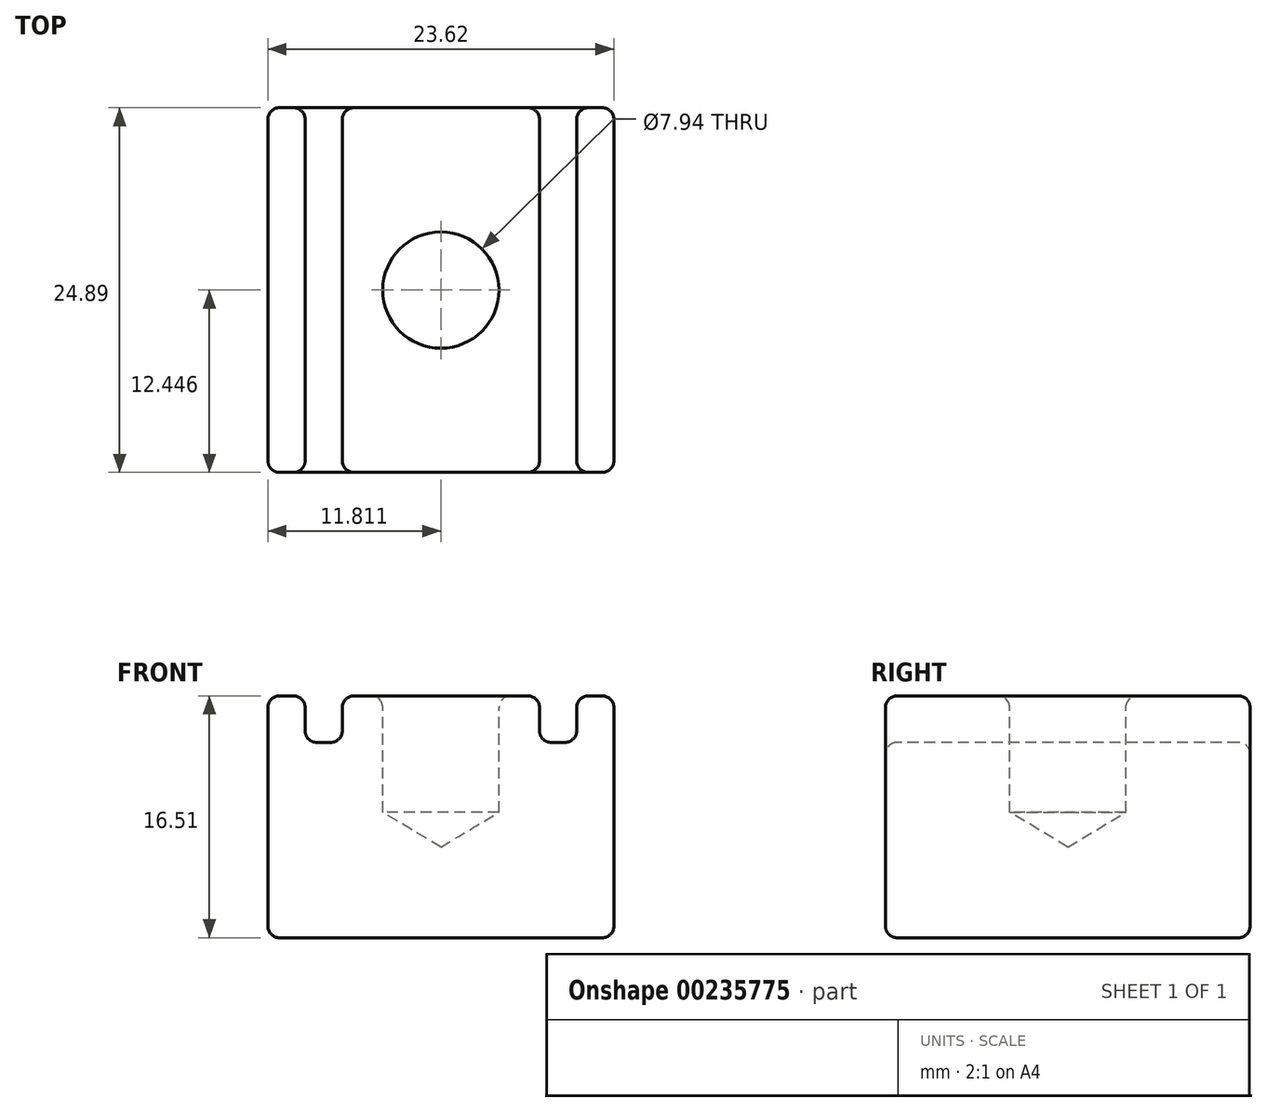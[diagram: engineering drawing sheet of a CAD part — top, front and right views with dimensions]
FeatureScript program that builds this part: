
annotation { "Feature Type Name" : "Feature", "Feature Type Description" : "" }
export const myFeature = defineFeature(function(context is Context, id is Id, definition is map)
    precondition{}
    {
        {
            var Q0;
            Q0=qCreatedBy(makeId("Top.planeOp"),FACE);
            var sketch = newSketch(context, id + "F0", { "sketchPlane" : qUnion([Q0])});
            skLineSegment(sketch, "E0.bottom", {"start": v(0.8, 0) * mm, "end": v(1.75, 0) * mm});
            skLineSegment(sketch, "E0.top", {"start": v(0.8, 24.9) * mm, "end": v(1.75, 24.9) * mm});
            skLineSegment(sketch, "E0.left", {"start": v(0, 0.8) * mm, "end": v(0, 24.1) * mm});
            skLineSegment(sketch, "E0.right", {"start": v(2.54, 0.8) * mm, "end": v(2.54, 24.1) * mm});
            skPoint(sketch, "E1.visualSharp", {"position": v(0, 24.9) * mm});
            skArc(sketch, "E1.filletArc", {"start": v(0.8, 24.9) * mm, "mid": v(0.23, 24.66) * mm, "end": v(0, 24.1) * mm});
            skPoint(sketch, "E2.visualSharp", {"position": v(0, 0) * mm});
            skArc(sketch, "E2.filletArc", {"start": v(0, 0.8) * mm, "mid": v(0.23, 0.23) * mm, "end": v(0.8, 0) * mm});
            skPoint(sketch, "E3.visualSharp", {"position": v(2.54, 24.9) * mm});
            skArc(sketch, "E3.filletArc", {"start": v(2.54, 24.1) * mm, "mid": v(2.3, 24.66) * mm, "end": v(1.75, 24.9) * mm});
            skPoint(sketch, "E4.visualSharp", {"position": v(2.54, 0) * mm});
            skArc(sketch, "E4.filletArc", {"start": v(1.75, 0) * mm, "mid": v(2.3, 0.23) * mm, "end": v(2.54, 0.8) * mm});
            skLineSegment(sketch, "E5.bottom", {"start": v(21.88, 0) * mm, "end": v(22.83, 0) * mm});
            skLineSegment(sketch, "E5.top", {"start": v(21.88, 24.9) * mm, "end": v(22.83, 24.9) * mm});
            skLineSegment(sketch, "E5.left", {"start": v(21.08, 0.8) * mm, "end": v(21.08, 24.1) * mm});
            skLineSegment(sketch, "E5.right", {"start": v(23.62, 0.8) * mm, "end": v(23.62, 24.1) * mm});
            skPoint(sketch, "E6.visualSharp", {"position": v(21.08, 24.9) * mm});
            skArc(sketch, "E6.filletArc", {"start": v(21.88, 24.9) * mm, "mid": v(21.31, 24.66) * mm, "end": v(21.08, 24.1) * mm});
            skPoint(sketch, "E7.visualSharp", {"position": v(21.08, 0) * mm});
            skArc(sketch, "E7.filletArc", {"start": v(21.08, 0.8) * mm, "mid": v(21.31, 0.23) * mm, "end": v(21.88, 0) * mm});
            skPoint(sketch, "E8.visualSharp", {"position": v(23.62, 24.9) * mm});
            skArc(sketch, "E8.filletArc", {"start": v(23.62, 24.1) * mm, "mid": v(23.39, 24.66) * mm, "end": v(22.83, 24.9) * mm});
            skPoint(sketch, "E9.visualSharp", {"position": v(23.62, 0) * mm});
            skArc(sketch, "E9.filletArc", {"start": v(22.83, 0) * mm, "mid": v(23.39, 0.23) * mm, "end": v(23.62, 0.8) * mm});
            skLineSegment(sketch, "E10.bottom", {"start": v(5.87, 24.9) * mm, "end": v(17.75, 24.9) * mm});
            skLineSegment(sketch, "E10.top", {"start": v(5.87, 0) * mm, "end": v(17.75, 0) * mm});
            skLineSegment(sketch, "E10.left", {"start": v(5.08, 24.1) * mm, "end": v(5.08, 0.8) * mm});
            skLineSegment(sketch, "E10.right", {"start": v(18.54, 24.1) * mm, "end": v(18.54, 0.8) * mm});
            skPoint(sketch, "E11.visualSharp", {"position": v(5.08, 24.9) * mm});
            skArc(sketch, "E11.filletArc", {"start": v(5.87, 24.9) * mm, "mid": v(5.31, 24.66) * mm, "end": v(5.08, 24.1) * mm});
            skPoint(sketch, "E12.visualSharp", {"position": v(18.54, 24.9) * mm});
            skArc(sketch, "E12.filletArc", {"start": v(18.54, 24.1) * mm, "mid": v(18.3, 24.66) * mm, "end": v(17.75, 24.9) * mm});
            skPoint(sketch, "E13.visualSharp", {"position": v(18.54, 0) * mm});
            skArc(sketch, "E13.filletArc", {"start": v(17.75, 0) * mm, "mid": v(18.3, 0.23) * mm, "end": v(18.54, 0.8) * mm});
            skPoint(sketch, "E14.visualSharp", {"position": v(5.08, 0) * mm});
            skArc(sketch, "E14.filletArc", {"start": v(5.08, 0.8) * mm, "mid": v(5.31, 0.23) * mm, "end": v(5.87, 0) * mm});
            skSolve(sketch);
        }
        {
            var Q0;
            Q0=qCreatedBy(makeId("Top.planeOp"),FACE);
            var sketch = newSketch(context, id + "F1", { "sketchPlane" : qUnion([Q0])});
            skLineSegment(sketch, "E15.bottom", {"start": v(0.8, 0) * mm, "end": v(22.83, 0) * mm});
            skLineSegment(sketch, "E15.top", {"start": v(0.8, 24.9) * mm, "end": v(22.83, 24.9) * mm});
            skLineSegment(sketch, "E15.left", {"start": v(0, 0.8) * mm, "end": v(0, 24.1) * mm});
            skLineSegment(sketch, "E15.right", {"start": v(23.62, 0.8) * mm, "end": v(23.62, 24.1) * mm});
            skPoint(sketch, "E16.visualSharp", {"position": v(0, 24.9) * mm});
            skArc(sketch, "E16.filletArc", {"start": v(0.8, 24.9) * mm, "mid": v(0.23, 24.66) * mm, "end": v(0, 24.1) * mm});
            skPoint(sketch, "E17.visualSharp", {"position": v(23.62, 24.9) * mm});
            skArc(sketch, "E17.filletArc", {"start": v(23.62, 24.1) * mm, "mid": v(23.39, 24.66) * mm, "end": v(22.83, 24.9) * mm});
            skPoint(sketch, "E18.visualSharp", {"position": v(23.62, 0) * mm});
            skArc(sketch, "E18.filletArc", {"start": v(22.83, 0) * mm, "mid": v(23.39, 0.23) * mm, "end": v(23.62, 0.8) * mm});
            skPoint(sketch, "E19.visualSharp", {"position": v(0, 0) * mm});
            skArc(sketch, "E19.filletArc", {"start": v(0, 0.8) * mm, "mid": v(0.23, 0.23) * mm, "end": v(0.8, 0) * mm});
            skSolve(sketch);
        }
        {
            var Q0;
            Q0 = qSketchRegion(id + "F1", true);
            extrude(context, id + "F2", {"entities" : qUnion([Q0]), "oppositeDirection" : true, "depth" : 13.33 * mm});
        }
        {
            var Q0;
            Q0 = qSketchRegion(id + "F0", true);
            extrude(context, id + "F3", {"entities" : qUnion([Q0]), "operationType" : NewBodyOperationType.ADD, "depth" : 3.17 * mm});
        }
        {
            var Q0;
            Q0=makeQuery(id+"F3.opExtrude","CAP_FACE",FACE,{"disambiguationData":[OSD([sQuery(id+"F0.wireOp",EDGE,"E10.bottom"),sQuery(id+"F0.wireOp",EDGE,"E10.top"),sQuery(id+"F0.wireOp",EDGE,"E10.left"),sQuery(id+"F0.wireOp",EDGE,"E10.right"),sQuery(id+"F0.wireOp",EDGE,"E11.filletArc"),sQuery(id+"F0.wireOp",EDGE,"E12.filletArc"),sQuery(id+"F0.wireOp",EDGE,"E13.filletArc"),sQuery(id+"F0.wireOp",EDGE,"E14.filletArc")])],"isStart":false});
            var sketch = newSketch(context, id + "F4", { "sketchPlane" : qUnion([Q0])});
            skCircle(sketch, "E20", {"center": v(11.81, 12.45) * mm, "radius": 3.97 * mm});
            skSolve(sketch);
        }
        {
            var Q0;
            Q0=sQuery(id+"F4.wireOp",VERTEX,"E20.center");
            var Q1;
            Q1=makeQuery(id+"F2.opExtrude","SWEPT_BODY",BODY,{"disambiguationData":[OSD([sQuery(id+"F1.wireOp",EDGE,"E15.bottom"),sQuery(id+"F1.wireOp",EDGE,"E15.top"),sQuery(id+"F1.wireOp",EDGE,"E15.left"),sQuery(id+"F1.wireOp",EDGE,"E15.right"),sQuery(id+"F1.wireOp",EDGE,"E16.filletArc"),sQuery(id+"F1.wireOp",EDGE,"E17.filletArc"),sQuery(id+"F1.wireOp",EDGE,"E18.filletArc"),sQuery(id+"F1.wireOp",EDGE,"E19.filletArc")])]});
            hole(context, id + "F5", {"style" : HoleStyle.SIMPLE, "endStyle" : HoleEndStyle.BLIND, "holeDiameter" : 7.94 * mm, "holeDepth" : 7.94 * mm, "locations" : qUnion([Q0]), "scope" : qUnion([Q1])});
        }
        {
            var Q0;
            Q0=makeQuery(id+"F3.opExtrude","CAP_FACE",FACE,{"disambiguationData":[OSD([sQuery(id+"F0.wireOp",EDGE,"E10.bottom"),sQuery(id+"F0.wireOp",EDGE,"E10.top"),sQuery(id+"F0.wireOp",EDGE,"E10.left"),sQuery(id+"F0.wireOp",EDGE,"E10.right"),sQuery(id+"F0.wireOp",EDGE,"E11.filletArc"),sQuery(id+"F0.wireOp",EDGE,"E12.filletArc"),sQuery(id+"F0.wireOp",EDGE,"E13.filletArc"),sQuery(id+"F0.wireOp",EDGE,"E14.filletArc")])],"isStart":false});
            var Q1;
            Q1=makeQuery(id+"F3.opExtrude","CAP_FACE",FACE,{"disambiguationData":[OSD([sQuery(id+"F0.wireOp",EDGE,"E5.bottom"),sQuery(id+"F0.wireOp",EDGE,"E5.top"),sQuery(id+"F0.wireOp",EDGE,"E5.left"),sQuery(id+"F0.wireOp",EDGE,"E5.right"),sQuery(id+"F0.wireOp",EDGE,"E6.filletArc"),sQuery(id+"F0.wireOp",EDGE,"E7.filletArc"),sQuery(id+"F0.wireOp",EDGE,"E8.filletArc"),sQuery(id+"F0.wireOp",EDGE,"E9.filletArc")])],"isStart":false});
            var Q2;
            Q2=makeQuery(id+"F3.opExtrude","CAP_FACE",FACE,{"disambiguationData":[OSD([sQuery(id+"F0.wireOp",EDGE,"E0.bottom"),sQuery(id+"F0.wireOp",EDGE,"E0.top"),sQuery(id+"F0.wireOp",EDGE,"E0.left"),sQuery(id+"F0.wireOp",EDGE,"E0.right"),sQuery(id+"F0.wireOp",EDGE,"E1.filletArc"),sQuery(id+"F0.wireOp",EDGE,"E2.filletArc"),sQuery(id+"F0.wireOp",EDGE,"E3.filletArc"),sQuery(id+"F0.wireOp",EDGE,"E4.filletArc")])],"isStart":false});
            var Q3;
            {var subQ0=sQuery(id+"F1.wireOp",EDGE,"E15.bottom");var subQ1=sQuery(id+"F1.wireOp",EDGE,"E15.top");Q3=makeQuery(id+"F3.boolean.opBoolean","SPLIT",FACE,{"disambiguationData":[TD([makeQuery(id+"F3.opExtrude","SWEPT_FACE",FACE,{"disambiguationData":[OSD([sQuery(id+"F0.wireOp",EDGE,"E0.right")])]})])],"derivedFrom":makeQuery(id+"F2.opExtrude","CAP_FACE",FACE,{"disambiguationData":[OSD([subQ0,subQ1,sQuery(id+"F1.wireOp",EDGE,"E15.left"),sQuery(id+"F1.wireOp",EDGE,"E15.right"),sQuery(id+"F1.wireOp",EDGE,"E16.filletArc"),sQuery(id+"F1.wireOp",EDGE,"E17.filletArc"),sQuery(id+"F1.wireOp",EDGE,"E18.filletArc"),sQuery(id+"F1.wireOp",EDGE,"E19.filletArc")])],"isStart":true})});}
            var Q4;
            {var subQ0=sQuery(id+"F1.wireOp",EDGE,"E15.bottom");var subQ1=sQuery(id+"F1.wireOp",EDGE,"E15.top");Q4=makeQuery(id+"F3.boolean.opBoolean","SPLIT",FACE,{"disambiguationData":[TD([makeQuery(id+"F3.opExtrude","SWEPT_FACE",FACE,{"disambiguationData":[OSD([sQuery(id+"F0.wireOp",EDGE,"E5.left")])]})])],"derivedFrom":makeQuery(id+"F2.opExtrude","CAP_FACE",FACE,{"disambiguationData":[OSD([subQ0,subQ1,sQuery(id+"F1.wireOp",EDGE,"E15.left"),sQuery(id+"F1.wireOp",EDGE,"E15.right"),sQuery(id+"F1.wireOp",EDGE,"E16.filletArc"),sQuery(id+"F1.wireOp",EDGE,"E17.filletArc"),sQuery(id+"F1.wireOp",EDGE,"E18.filletArc"),sQuery(id+"F1.wireOp",EDGE,"E19.filletArc")])],"isStart":true})});}
            fillet(context, id + "F6", {"entities" : qUnion([Q0, Q1, Q2, Q3, Q4]), "radius" : 0.8 * mm, "tangentPropagation" : true, "allowEdgeOverflow" : false});
        }
        {
            var Q0;
            Q0=makeQuery(id+"F2.opExtrude","CAP_FACE",FACE,{"disambiguationData":[OSD([sQuery(id+"F1.wireOp",EDGE,"E15.bottom"),sQuery(id+"F1.wireOp",EDGE,"E15.top"),sQuery(id+"F1.wireOp",EDGE,"E15.left"),sQuery(id+"F1.wireOp",EDGE,"E15.right"),sQuery(id+"F1.wireOp",EDGE,"E16.filletArc"),sQuery(id+"F1.wireOp",EDGE,"E17.filletArc"),sQuery(id+"F1.wireOp",EDGE,"E18.filletArc"),sQuery(id+"F1.wireOp",EDGE,"E19.filletArc")])],"isStart":false});
            fillet(context, id + "F7", {"entities" : qUnion([Q0]), "radius" : 0.8 * mm, "tangentPropagation" : true, "allowEdgeOverflow" : false});
        }
    });
